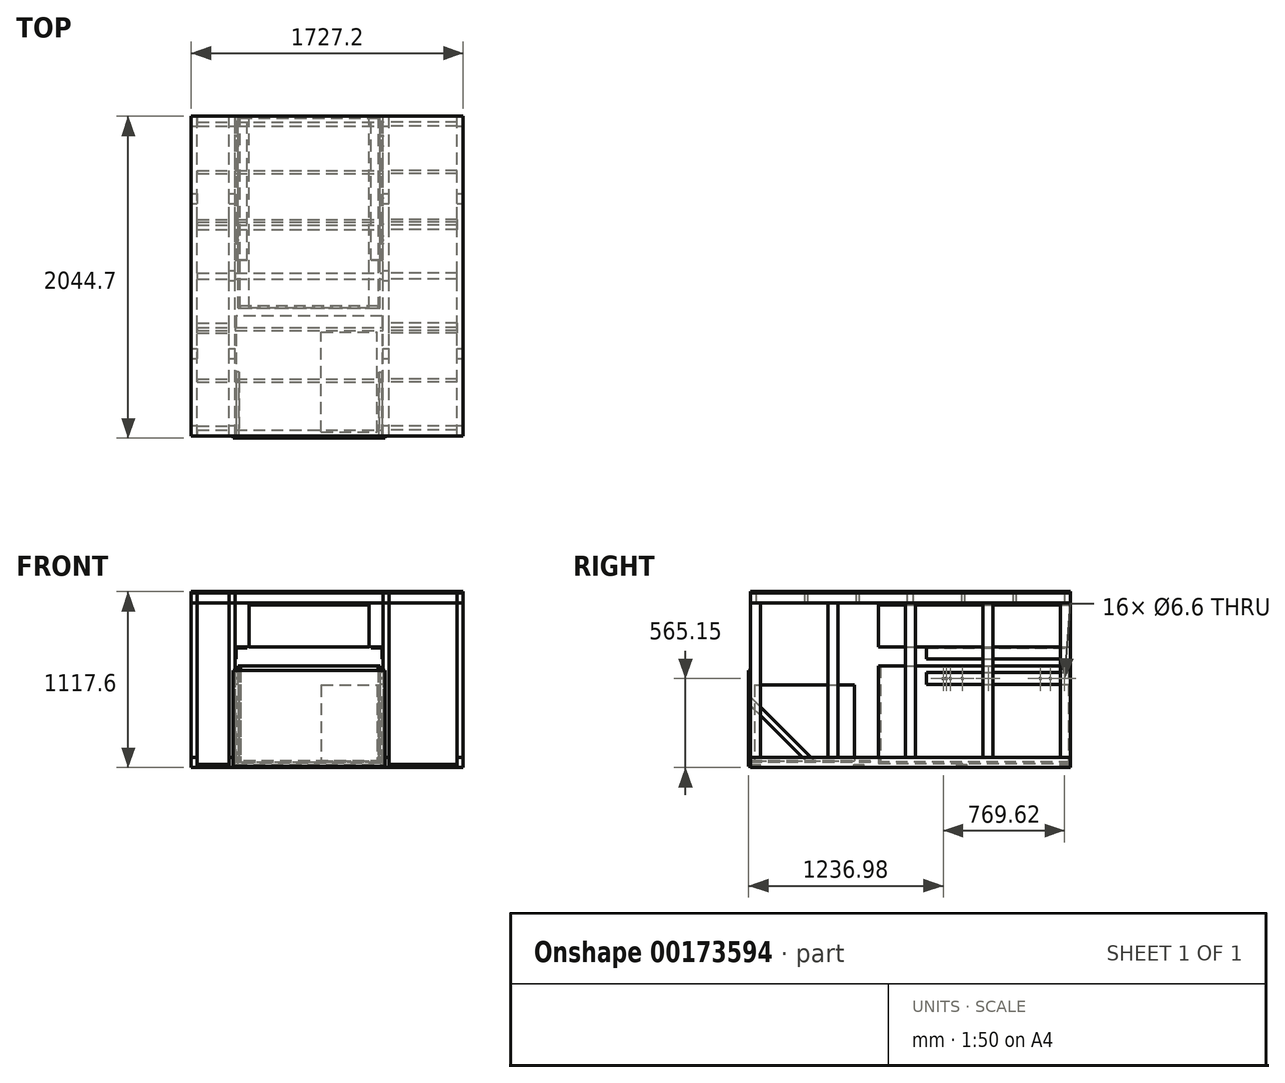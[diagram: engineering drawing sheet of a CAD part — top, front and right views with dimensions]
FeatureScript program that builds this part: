
annotation { "Feature Type Name" : "Feature", "Feature Type Description" : "" }
export const myFeature = defineFeature(function(context is Context, id is Id, definition is map)
    precondition{}
    {
        {
            var Q0;
            Q0=qCreatedBy(makeId("Top.planeOp"),FACE);
            cPlane(context, id + "F0", {"entities" : qUnion([Q0]), "cplaneType" : CPlaneType.OFFSET, "offset" : 1117.6 * mm, "width" : 152.4 * mm, "height" : 152.4 * mm});
        }
        {
            var Q0;
            Q0=qCreatedBy(id+"F0.planeOp",FACE);
            var sketch = newSketch(context, id + "F1", { "sketchPlane" : qUnion([Q0])});
            skLineSegment(sketch, "E0.bottom", {"start": v(-863.6, 1016) * mm, "end": v(863.6, 1016) * mm});
            skLineSegment(sketch, "E0.top", {"start": v(-863.6, -1016) * mm, "end": v(863.6, -1016) * mm});
            skLineSegment(sketch, "E0.left", {"start": v(-863.6, 1016) * mm, "end": v(-863.6, -1016) * mm});
            skLineSegment(sketch, "E0.right", {"start": v(863.6, 1016) * mm, "end": v(863.6, -1016) * mm});
            skPoint(sketch, "E0.middle", {"position": v(0, 0) * mm});
            skSolve(sketch);
        }
        {
            var Q0;
            Q0=makeQuery(id+"F1.imprint","IMPRINT",FACE,{"disambiguationData":[TD([[makeQuery(id+"F1.imprint","IMPRINT",EDGE,{"derivedFrom":sQuery(id+"F1.wireOp",EDGE,"E0.bottom")}),-1.0]])]});
            extrude(context, id + "F2", {"entities" : qUnion([Q0]), "oppositeDirection" : true, "depth" : 9.52 * mm});
        }
        {
            var Q0;
            Q0=makeQuery(id+"F2.opExtrude","SWEPT_FACE",FACE,{"disambiguationData":[OSD([sQuery(id+"F1.wireOp",EDGE,"E0.bottom")])]});
            var sketch = newSketch(context, id + "F3", { "sketchPlane" : qUnion([Q0])});
            skLineSegment(sketch, "E1.bottom", {"start": v(-863.6, 1108.08) * mm, "end": v(-825.5, 1108.08) * mm});
            skLineSegment(sketch, "E1.top", {"start": v(-863.6, 1044.58) * mm, "end": v(-825.5, 1044.58) * mm});
            skLineSegment(sketch, "E1.left", {"start": v(-863.6, 1108.08) * mm, "end": v(-863.6, 1044.58) * mm});
            skLineSegment(sketch, "E1.right", {"start": v(-825.5, 1108.08) * mm, "end": v(-825.5, 1044.58) * mm});
            skLineSegment(sketch, "E2.bottom", {"start": v(863.6, 1108.08) * mm, "end": v(825.5, 1108.08) * mm});
            skLineSegment(sketch, "E2.top", {"start": v(863.6, 1044.58) * mm, "end": v(825.5, 1044.58) * mm});
            skLineSegment(sketch, "E2.left", {"start": v(863.6, 1108.08) * mm, "end": v(863.6, 1044.58) * mm});
            skLineSegment(sketch, "E2.right", {"start": v(825.5, 1108.08) * mm, "end": v(825.5, 1044.58) * mm});
            skLineSegment(sketch, "E3.bottom", {"start": v(-863.6, 0) * mm, "end": v(-825.5, 0) * mm});
            skLineSegment(sketch, "E3.top", {"start": v(-863.6, 63.5) * mm, "end": v(-825.5, 63.5) * mm});
            skLineSegment(sketch, "E3.left", {"start": v(-863.6, 0) * mm, "end": v(-863.6, 63.5) * mm});
            skLineSegment(sketch, "E3.right", {"start": v(-825.5, 0) * mm, "end": v(-825.5, 63.5) * mm});
            skLineSegment(sketch, "E4.bottom", {"start": v(863.6, 0) * mm, "end": v(825.5, 0) * mm});
            skLineSegment(sketch, "E4.top", {"start": v(863.6, 63.5) * mm, "end": v(825.5, 63.5) * mm});
            skLineSegment(sketch, "E4.left", {"start": v(863.6, 0) * mm, "end": v(863.6, 63.5) * mm});
            skLineSegment(sketch, "E4.right", {"start": v(825.5, 0) * mm, "end": v(825.5, 63.5) * mm});
            skLineSegment(sketch, "E5.bottom", {"start": v(-355.6, 1108.08) * mm, "end": v(-393.7, 1108.08) * mm});
            skLineSegment(sketch, "E5.top", {"start": v(-355.6, 1044.58) * mm, "end": v(-393.7, 1044.58) * mm});
            skLineSegment(sketch, "E5.left", {"start": v(-355.6, 1108.08) * mm, "end": v(-355.6, 1044.58) * mm});
            skLineSegment(sketch, "E5.right", {"start": v(-393.7, 1108.08) * mm, "end": v(-393.7, 1044.58) * mm});
            skLineSegment(sketch, "E6.bottom", {"start": v(584.2, 1108.08) * mm, "end": v(622.3, 1108.08) * mm});
            skLineSegment(sketch, "E6.top", {"start": v(584.2, 1044.58) * mm, "end": v(622.3, 1044.58) * mm});
            skLineSegment(sketch, "E6.left", {"start": v(584.2, 1108.08) * mm, "end": v(584.2, 1044.58) * mm});
            skLineSegment(sketch, "E6.right", {"start": v(622.3, 1108.08) * mm, "end": v(622.3, 1044.58) * mm});
            skLineSegment(sketch, "E7.bottom", {"start": v(-355.6, 0) * mm, "end": v(-393.7, 0) * mm});
            skLineSegment(sketch, "E7.top", {"start": v(-355.6, 63.5) * mm, "end": v(-393.7, 63.5) * mm});
            skLineSegment(sketch, "E7.left", {"start": v(-355.6, 0) * mm, "end": v(-355.6, 63.5) * mm});
            skLineSegment(sketch, "E7.right", {"start": v(-393.7, 0) * mm, "end": v(-393.7, 63.5) * mm});
            skLineSegment(sketch, "E8.bottom", {"start": v(622.3, 0) * mm, "end": v(584.2, 0) * mm});
            skLineSegment(sketch, "E8.top", {"start": v(622.3, 63.5) * mm, "end": v(584.2, 63.5) * mm});
            skLineSegment(sketch, "E8.left", {"start": v(622.3, 0) * mm, "end": v(622.3, 63.5) * mm});
            skLineSegment(sketch, "E8.right", {"start": v(584.2, 0) * mm, "end": v(584.2, 63.5) * mm});
            skSolve(sketch);
        }
        {
            var Q0;
            Q0 = qSketchRegion(id + "F3", true);
            var Q1;
            Q1=makeQuery(id+"F2.opExtrude","SWEPT_FACE",FACE,{"disambiguationData":[OSD([sQuery(id+"F1.wireOp",EDGE,"E0.top")])]});
            extrude(context, id + "F4", {"entities" : qUnion([Q0]), "endBound" : BoundingType.UP_TO_SURFACE, "oppositeDirection" : true, "endBoundEntityFace" : qUnion([Q1]), "depth" : 25.4 * mm});
        }
        {
            var Q0;
            Q0=makeQuery(id+"F4.opExtrude","SWEPT_FACE",FACE,{"disambiguationData":[OSD([sQuery(id+"F3.wireOp",EDGE,"E4.top")])]});
            var sketch = newSketch(context, id + "F5", { "sketchPlane" : qUnion([Q0])});
            skLineSegment(sketch, "E9.bottom", {"start": v(863.6, 1016) * mm, "end": v(825.5, 1016) * mm});
            skLineSegment(sketch, "E9.top", {"start": v(863.6, 952.5) * mm, "end": v(825.5, 952.5) * mm});
            skLineSegment(sketch, "E9.left", {"start": v(863.6, 1016) * mm, "end": v(863.6, 952.5) * mm});
            skLineSegment(sketch, "E9.right", {"start": v(825.5, 1016) * mm, "end": v(825.5, 952.5) * mm});
            skLineSegment(sketch, "E10.bottom", {"start": v(863.6, 523.87) * mm, "end": v(825.5, 523.87) * mm});
            skLineSegment(sketch, "E10.top", {"start": v(863.6, 460.37) * mm, "end": v(825.5, 460.37) * mm});
            skLineSegment(sketch, "E10.left", {"start": v(863.6, 523.87) * mm, "end": v(863.6, 460.37) * mm});
            skLineSegment(sketch, "E10.right", {"start": v(825.5, 523.87) * mm, "end": v(825.5, 460.37) * mm});
            skLineSegment(sketch, "E11.bottom", {"start": v(825.5, 31.75) * mm, "end": v(863.6, 31.75) * mm, "construction": true});
            skLineSegment(sketch, "E11.top", {"start": v(825.5, -31.75) * mm, "end": v(863.6, -31.75) * mm, "construction": true});
            skLineSegment(sketch, "E11.left", {"start": v(825.5, 31.75) * mm, "end": v(825.5, -31.75) * mm, "construction": true});
            skLineSegment(sketch, "E11.right", {"start": v(863.6, 31.75) * mm, "end": v(863.6, -31.75) * mm, "construction": true});
            skLineSegment(sketch, "E12.bottom", {"start": v(863.6, -460.38) * mm, "end": v(825.5, -460.38) * mm});
            skLineSegment(sketch, "E12.top", {"start": v(863.6, -523.88) * mm, "end": v(825.5, -523.88) * mm});
            skLineSegment(sketch, "E12.left", {"start": v(863.6, -460.38) * mm, "end": v(863.6, -523.88) * mm});
            skLineSegment(sketch, "E12.right", {"start": v(825.5, -460.38) * mm, "end": v(825.5, -523.88) * mm});
            skLineSegment(sketch, "E13.bottom", {"start": v(825.5, -952.5) * mm, "end": v(863.6, -952.5) * mm});
            skLineSegment(sketch, "E13.top", {"start": v(825.5, -1016) * mm, "end": v(863.6, -1016) * mm});
            skLineSegment(sketch, "E13.left", {"start": v(825.5, -952.5) * mm, "end": v(825.5, -1016) * mm});
            skLineSegment(sketch, "E13.right", {"start": v(863.6, -952.5) * mm, "end": v(863.6, -1016) * mm});
            skLineSegment(sketch, "E14", {"start": v(863.6, 952.5) * mm, "end": v(863.6, 523.87) * mm, "construction": true});
            skLineSegment(sketch, "E15", {"start": v(863.6, 460.37) * mm, "end": v(863.6, 31.75) * mm, "construction": true});
            skLineSegment(sketch, "E16", {"start": v(863.6, -31.75) * mm, "end": v(863.6, -460.38) * mm, "construction": true});
            skLineSegment(sketch, "E17", {"start": v(863.6, -523.88) * mm, "end": v(863.6, -952.5) * mm, "construction": true});
            skPoint(sketch, "E18.0", {"position": v(863.6, 1016) * mm});
            skPoint(sketch, "E18.1", {"position": v(825.5, 1016) * mm});
            skPoint(sketch, "E18.2", {"position": v(863.6, -1016) * mm});
            skPoint(sketch, "E18.3", {"position": v(825.5, -1016) * mm});
            skLineSegment(sketch, "E19.bottom", {"start": v(393.7, 1016) * mm, "end": v(355.6, 1016) * mm});
            skLineSegment(sketch, "E19.top", {"start": v(393.7, 952.5) * mm, "end": v(355.6, 952.5) * mm});
            skLineSegment(sketch, "E19.left", {"start": v(393.7, 1016) * mm, "end": v(393.7, 952.5) * mm});
            skLineSegment(sketch, "E19.right", {"start": v(355.6, 1016) * mm, "end": v(355.6, 952.5) * mm});
            skLineSegment(sketch, "E20.bottom", {"start": v(393.7, 523.87) * mm, "end": v(355.6, 523.87) * mm});
            skLineSegment(sketch, "E20.top", {"start": v(393.7, 460.37) * mm, "end": v(355.6, 460.37) * mm});
            skLineSegment(sketch, "E20.left", {"start": v(393.7, 523.87) * mm, "end": v(393.7, 460.37) * mm});
            skLineSegment(sketch, "E20.right", {"start": v(355.6, 523.87) * mm, "end": v(355.6, 460.37) * mm});
            skLineSegment(sketch, "E21.bottom", {"start": v(355.6, 31.75) * mm, "end": v(393.7, 31.75) * mm});
            skLineSegment(sketch, "E21.top", {"start": v(355.6, -31.75) * mm, "end": v(393.7, -31.75) * mm});
            skLineSegment(sketch, "E21.left", {"start": v(355.6, 31.75) * mm, "end": v(355.6, -31.75) * mm});
            skLineSegment(sketch, "E21.right", {"start": v(393.7, 31.75) * mm, "end": v(393.7, -31.75) * mm});
            skLineSegment(sketch, "E22.bottom", {"start": v(393.7, -460.38) * mm, "end": v(355.6, -460.38) * mm});
            skLineSegment(sketch, "E22.top", {"start": v(393.7, -523.88) * mm, "end": v(355.6, -523.88) * mm});
            skLineSegment(sketch, "E22.left", {"start": v(393.7, -460.38) * mm, "end": v(393.7, -523.88) * mm});
            skLineSegment(sketch, "E22.right", {"start": v(355.6, -460.38) * mm, "end": v(355.6, -523.88) * mm});
            skLineSegment(sketch, "E23.bottom", {"start": v(355.6, -952.5) * mm, "end": v(393.7, -952.5) * mm});
            skLineSegment(sketch, "E23.top", {"start": v(355.6, -1016) * mm, "end": v(393.7, -1016) * mm});
            skLineSegment(sketch, "E23.left", {"start": v(355.6, -952.5) * mm, "end": v(355.6, -1016) * mm});
            skLineSegment(sketch, "E23.right", {"start": v(393.7, -952.5) * mm, "end": v(393.7, -1016) * mm});
            skLineSegment(sketch, "E24", {"start": v(393.7, 952.5) * mm, "end": v(393.7, 523.87) * mm, "construction": true});
            skLineSegment(sketch, "E25", {"start": v(393.7, 460.37) * mm, "end": v(393.7, 31.75) * mm, "construction": true});
            skLineSegment(sketch, "E26", {"start": v(393.7, -31.75) * mm, "end": v(393.7, -460.38) * mm, "construction": true});
            skLineSegment(sketch, "E27", {"start": v(393.7, -523.88) * mm, "end": v(393.7, -952.5) * mm, "construction": true});
            skPoint(sketch, "E28.0", {"position": v(393.7, 1016) * mm});
            skPoint(sketch, "E28.3", {"position": v(355.6, -1016) * mm});
            skPoint(sketch, "E29.0", {"position": v(393.7, -1016) * mm});
            skPoint(sketch, "E29.3", {"position": v(355.6, 1016) * mm});
            skPoint(sketch, "E29.4", {"position": v(-584.2, 1016) * mm});
            skPoint(sketch, "E29.5", {"position": v(-622.3, 1016) * mm});
            skPoint(sketch, "E29.6", {"position": v(-825.5, 1016) * mm});
            skPoint(sketch, "E29.7", {"position": v(-863.6, 1016) * mm});
            skPoint(sketch, "E29.8", {"position": v(-584.2, -1016) * mm});
            skPoint(sketch, "E29.9", {"position": v(-622.3, -1016) * mm});
            skPoint(sketch, "E29.10", {"position": v(-825.5, -1016) * mm});
            skPoint(sketch, "E29.11", {"position": v(-863.6, -1016) * mm});
            skLineSegment(sketch, "E30.bottom", {"start": v(-584.2, 1016) * mm, "end": v(-622.3, 1016) * mm});
            skLineSegment(sketch, "E30.top", {"start": v(-584.2, 952.5) * mm, "end": v(-622.3, 952.5) * mm});
            skLineSegment(sketch, "E30.left", {"start": v(-584.2, 1016) * mm, "end": v(-584.2, 952.5) * mm});
            skLineSegment(sketch, "E30.right", {"start": v(-622.3, 1016) * mm, "end": v(-622.3, 952.5) * mm});
            skLineSegment(sketch, "E31.bottom", {"start": v(-584.2, 523.87) * mm, "end": v(-622.3, 523.87) * mm});
            skLineSegment(sketch, "E31.top", {"start": v(-584.2, 460.37) * mm, "end": v(-622.3, 460.37) * mm});
            skLineSegment(sketch, "E31.left", {"start": v(-584.2, 523.87) * mm, "end": v(-584.2, 460.37) * mm});
            skLineSegment(sketch, "E31.right", {"start": v(-622.3, 523.87) * mm, "end": v(-622.3, 460.37) * mm});
            skLineSegment(sketch, "E32.bottom", {"start": v(-622.3, 31.75) * mm, "end": v(-584.2, 31.75) * mm});
            skLineSegment(sketch, "E32.top", {"start": v(-622.3, -31.75) * mm, "end": v(-584.2, -31.75) * mm});
            skLineSegment(sketch, "E32.left", {"start": v(-622.3, 31.75) * mm, "end": v(-622.3, -31.75) * mm});
            skLineSegment(sketch, "E32.right", {"start": v(-584.2, 31.75) * mm, "end": v(-584.2, -31.75) * mm});
            skLineSegment(sketch, "E33.bottom", {"start": v(-584.2, -460.38) * mm, "end": v(-622.3, -460.38) * mm});
            skLineSegment(sketch, "E33.top", {"start": v(-584.2, -523.88) * mm, "end": v(-622.3, -523.88) * mm});
            skLineSegment(sketch, "E33.left", {"start": v(-584.2, -460.38) * mm, "end": v(-584.2, -523.88) * mm});
            skLineSegment(sketch, "E33.right", {"start": v(-622.3, -460.38) * mm, "end": v(-622.3, -523.88) * mm});
            skLineSegment(sketch, "E34.bottom", {"start": v(-622.3, -952.5) * mm, "end": v(-584.2, -952.5) * mm});
            skLineSegment(sketch, "E34.top", {"start": v(-622.3, -1016) * mm, "end": v(-584.2, -1016) * mm});
            skLineSegment(sketch, "E34.left", {"start": v(-622.3, -952.5) * mm, "end": v(-622.3, -1016) * mm});
            skLineSegment(sketch, "E34.right", {"start": v(-584.2, -952.5) * mm, "end": v(-584.2, -1016) * mm});
            skLineSegment(sketch, "E35", {"start": v(-584.2, 952.5) * mm, "end": v(-584.2, 523.87) * mm, "construction": true});
            skLineSegment(sketch, "E36", {"start": v(-584.2, 460.37) * mm, "end": v(-584.2, 31.75) * mm, "construction": true});
            skLineSegment(sketch, "E37", {"start": v(-584.2, -31.75) * mm, "end": v(-584.2, -460.38) * mm, "construction": true});
            skLineSegment(sketch, "E38", {"start": v(-584.2, -523.88) * mm, "end": v(-584.2, -952.5) * mm, "construction": true});
            skLineSegment(sketch, "E39.bottom", {"start": v(-825.5, 1016) * mm, "end": v(-863.6, 1016) * mm});
            skLineSegment(sketch, "E39.top", {"start": v(-825.5, 952.5) * mm, "end": v(-863.6, 952.5) * mm});
            skLineSegment(sketch, "E39.left", {"start": v(-825.5, 1016) * mm, "end": v(-825.5, 952.5) * mm});
            skLineSegment(sketch, "E39.right", {"start": v(-863.6, 1016) * mm, "end": v(-863.6, 952.5) * mm});
            skLineSegment(sketch, "E40.bottom", {"start": v(-825.5, 523.87) * mm, "end": v(-863.6, 523.87) * mm});
            skLineSegment(sketch, "E40.top", {"start": v(-825.5, 460.37) * mm, "end": v(-863.6, 460.37) * mm});
            skLineSegment(sketch, "E40.left", {"start": v(-825.5, 523.87) * mm, "end": v(-825.5, 460.37) * mm});
            skLineSegment(sketch, "E40.right", {"start": v(-863.6, 523.87) * mm, "end": v(-863.6, 460.37) * mm});
            skLineSegment(sketch, "E41.bottom", {"start": v(-863.6, 31.75) * mm, "end": v(-825.5, 31.75) * mm, "construction": true});
            skLineSegment(sketch, "E41.top", {"start": v(-863.6, -31.75) * mm, "end": v(-825.5, -31.75) * mm, "construction": true});
            skLineSegment(sketch, "E41.left", {"start": v(-863.6, 31.75) * mm, "end": v(-863.6, -31.75) * mm, "construction": true});
            skLineSegment(sketch, "E41.right", {"start": v(-825.5, 31.75) * mm, "end": v(-825.5, -31.75) * mm, "construction": true});
            skLineSegment(sketch, "E42.bottom", {"start": v(-825.5, -460.38) * mm, "end": v(-863.6, -460.38) * mm});
            skLineSegment(sketch, "E42.top", {"start": v(-825.5, -523.88) * mm, "end": v(-863.6, -523.88) * mm});
            skLineSegment(sketch, "E42.left", {"start": v(-825.5, -460.38) * mm, "end": v(-825.5, -523.88) * mm});
            skLineSegment(sketch, "E42.right", {"start": v(-863.6, -460.38) * mm, "end": v(-863.6, -523.88) * mm});
            skLineSegment(sketch, "E43.bottom", {"start": v(-863.6, -952.5) * mm, "end": v(-825.5, -952.5) * mm});
            skLineSegment(sketch, "E43.top", {"start": v(-863.6, -1016) * mm, "end": v(-825.5, -1016) * mm});
            skLineSegment(sketch, "E43.left", {"start": v(-863.6, -952.5) * mm, "end": v(-863.6, -1016) * mm});
            skLineSegment(sketch, "E43.right", {"start": v(-825.5, -952.5) * mm, "end": v(-825.5, -1016) * mm});
            skLineSegment(sketch, "E44", {"start": v(-825.5, 952.5) * mm, "end": v(-825.5, 523.87) * mm, "construction": true});
            skLineSegment(sketch, "E45", {"start": v(-825.5, 460.37) * mm, "end": v(-825.5, 31.75) * mm, "construction": true});
            skLineSegment(sketch, "E46", {"start": v(-825.5, -31.75) * mm, "end": v(-825.5, -460.38) * mm, "construction": true});
            skLineSegment(sketch, "E47", {"start": v(-825.5, -523.88) * mm, "end": v(-825.5, -952.5) * mm, "construction": true});
            skSolve(sketch);
        }
        {
            var Q0;
            Q0 = qSketchRegion(id + "F5", true);
            var Q1;
            Q1=makeQuery(id+"F4.opExtrude","SWEPT_FACE",FACE,{"disambiguationData":[OSD([sQuery(id+"F3.wireOp",EDGE,"E6.top")])]});
            extrude(context, id + "F6", {"entities" : qUnion([Q0]), "endBound" : BoundingType.UP_TO_SURFACE, "endBoundEntityFace" : qUnion([Q1]), "depth" : 25.4 * mm});
        }
        {
            var Q0;
            Q0=makeQuery(id+"F4.opExtrude","SWEPT_FACE",FACE,{"disambiguationData":[OSD([sQuery(id+"F3.wireOp",EDGE,"E7.left")])]});
            var sketch = newSketch(context, id + "F7", { "sketchPlane" : qUnion([Q0])});
            skLineSegment(sketch, "E48.bottom", {"start": v(1016, 0) * mm, "end": v(952.5, 0) * mm, "construction": true});
            skLineSegment(sketch, "E48.top", {"start": v(1016, 19.05) * mm, "end": v(952.5, 19.05) * mm, "construction": true});
            skLineSegment(sketch, "E48.left", {"start": v(1016, 0) * mm, "end": v(1016, 19.05) * mm, "construction": true});
            skLineSegment(sketch, "E48.right", {"start": v(952.5, 0) * mm, "end": v(952.5, 19.05) * mm, "construction": true});
            skLineSegment(sketch, "E49.bottom", {"start": v(359.83, 0) * mm, "end": v(296.33, 0) * mm, "construction": true});
            skLineSegment(sketch, "E49.top", {"start": v(359.83, 19.05) * mm, "end": v(296.33, 19.05) * mm, "construction": true});
            skLineSegment(sketch, "E49.left", {"start": v(359.83, 0) * mm, "end": v(359.83, 19.05) * mm, "construction": true});
            skLineSegment(sketch, "E49.right", {"start": v(296.33, 0) * mm, "end": v(296.33, 19.05) * mm, "construction": true});
            skLineSegment(sketch, "E50.bottom", {"start": v(-296.33, 0) * mm, "end": v(-359.83, 0) * mm});
            skLineSegment(sketch, "E50.top", {"start": v(-296.33, 19.05) * mm, "end": v(-359.83, 19.05) * mm});
            skLineSegment(sketch, "E50.left", {"start": v(-296.33, 0) * mm, "end": v(-296.33, 19.05) * mm});
            skLineSegment(sketch, "E50.right", {"start": v(-359.83, 0) * mm, "end": v(-359.83, 19.05) * mm});
            skLineSegment(sketch, "E51.bottom", {"start": v(-952.5, 0) * mm, "end": v(-1016, 0) * mm});
            skLineSegment(sketch, "E51.top", {"start": v(-952.5, 19.05) * mm, "end": v(-1016, 19.05) * mm});
            skLineSegment(sketch, "E51.left", {"start": v(-952.5, 0) * mm, "end": v(-952.5, 19.05) * mm});
            skLineSegment(sketch, "E51.right", {"start": v(-1016, 0) * mm, "end": v(-1016, 19.05) * mm});
            skLineSegment(sketch, "E52", {"start": v(952.5, 0) * mm, "end": v(359.83, 0) * mm, "construction": true});
            skLineSegment(sketch, "E53", {"start": v(296.33, 0) * mm, "end": v(-296.33, 0) * mm, "construction": true});
            skLineSegment(sketch, "E54", {"start": v(-952.5, 0) * mm, "end": v(-359.83, 0) * mm, "construction": true});
            skPoint(sketch, "E55.0", {"position": v(1016, 1108.07) * mm});
            skLineSegment(sketch, "E56.bottom", {"start": v(1016, 1108.07) * mm, "end": v(977.9, 1108.07) * mm});
            skLineSegment(sketch, "E56.top", {"start": v(1016, 1044.58) * mm, "end": v(977.9, 1044.58) * mm});
            skLineSegment(sketch, "E56.left", {"start": v(1016, 1108.07) * mm, "end": v(1016, 1044.58) * mm});
            skLineSegment(sketch, "E56.right", {"start": v(977.9, 1108.07) * mm, "end": v(977.9, 1044.57) * mm});
            skLineSegment(sketch, "E57.bottom", {"start": v(670.98, 1108.07) * mm, "end": v(651.93, 1108.07) * mm});
            skLineSegment(sketch, "E57.top", {"start": v(670.98, 1044.57) * mm, "end": v(651.93, 1044.57) * mm});
            skLineSegment(sketch, "E57.left", {"start": v(670.98, 1108.07) * mm, "end": v(670.98, 1044.57) * mm});
            skLineSegment(sketch, "E57.right", {"start": v(651.93, 1108.07) * mm, "end": v(651.93, 1044.57) * mm});
            skLineSegment(sketch, "E58.bottom", {"start": v(345.02, 1044.57) * mm, "end": v(325.97, 1044.57) * mm});
            skLineSegment(sketch, "E58.top", {"start": v(345.02, 1108.07) * mm, "end": v(325.97, 1108.07) * mm});
            skLineSegment(sketch, "E58.left", {"start": v(345.02, 1044.57) * mm, "end": v(345.02, 1108.07) * mm});
            skLineSegment(sketch, "E58.right", {"start": v(325.97, 1044.57) * mm, "end": v(325.97, 1108.07) * mm});
            skLineSegment(sketch, "E59.bottom", {"start": v(19.05, 1108.07) * mm, "end": v(-19.05, 1108.07) * mm});
            skLineSegment(sketch, "E59.top", {"start": v(19.05, 1044.57) * mm, "end": v(-19.05, 1044.57) * mm});
            skLineSegment(sketch, "E59.left", {"start": v(19.05, 1108.07) * mm, "end": v(19.05, 1044.57) * mm});
            skLineSegment(sketch, "E59.right", {"start": v(-19.05, 1108.07) * mm, "end": v(-19.05, 1044.57) * mm});
            skLineSegment(sketch, "E60.bottom", {"start": v(-325.97, 1108.07) * mm, "end": v(-345.02, 1108.07) * mm});
            skLineSegment(sketch, "E60.top", {"start": v(-325.97, 1044.57) * mm, "end": v(-345.02, 1044.57) * mm});
            skLineSegment(sketch, "E60.left", {"start": v(-325.97, 1108.07) * mm, "end": v(-325.97, 1044.57) * mm});
            skLineSegment(sketch, "E60.right", {"start": v(-345.02, 1108.07) * mm, "end": v(-345.02, 1044.57) * mm});
            skLineSegment(sketch, "E61.bottom", {"start": v(-651.93, 1108.07) * mm, "end": v(-670.98, 1108.07) * mm});
            skLineSegment(sketch, "E61.top", {"start": v(-651.93, 1044.57) * mm, "end": v(-670.98, 1044.57) * mm});
            skLineSegment(sketch, "E61.left", {"start": v(-651.93, 1108.07) * mm, "end": v(-651.93, 1044.57) * mm});
            skLineSegment(sketch, "E61.right", {"start": v(-670.98, 1108.07) * mm, "end": v(-670.98, 1044.57) * mm});
            skLineSegment(sketch, "E62.bottom", {"start": v(-977.9, 1108.07) * mm, "end": v(-1016, 1108.07) * mm});
            skLineSegment(sketch, "E62.top", {"start": v(-977.9, 1044.57) * mm, "end": v(-1016, 1044.57) * mm});
            skLineSegment(sketch, "E62.left", {"start": v(-977.9, 1108.07) * mm, "end": v(-977.9, 1044.58) * mm});
            skLineSegment(sketch, "E62.right", {"start": v(-1016, 1108.07) * mm, "end": v(-1016, 1044.58) * mm});
            skLineSegment(sketch, "E63", {"start": v(977.9, 1108.07) * mm, "end": v(670.98, 1108.07) * mm, "construction": true});
            skLineSegment(sketch, "E64", {"start": v(651.93, 1108.07) * mm, "end": v(345.02, 1108.07) * mm, "construction": true});
            skLineSegment(sketch, "E65", {"start": v(325.97, 1108.07) * mm, "end": v(19.05, 1108.07) * mm, "construction": true});
            skLineSegment(sketch, "E66", {"start": v(-19.05, 1108.07) * mm, "end": v(-325.97, 1108.07) * mm, "construction": true});
            skLineSegment(sketch, "E67", {"start": v(-345.02, 1108.07) * mm, "end": v(-651.93, 1108.07) * mm, "construction": true});
            skLineSegment(sketch, "E68", {"start": v(-670.98, 1108.07) * mm, "end": v(-977.9, 1108.07) * mm, "construction": true});
            skPoint(sketch, "E69.0", {"position": v(-1016, 1108.07) * mm});
            skSolve(sketch);
        }
        {
            var Q0;
            Q0 = qSketchRegion(id + "F7", true);
            extrude(context, id + "F8", {"entities" : qUnion([Q0]), "endBound" : BoundingType.UP_TO_NEXT, "depth" : 25.4 * mm});
        }
        {
            var Q0;
            Q0=makeQuery(id+"F4.opExtrude","SWEPT_FACE",FACE,{"disambiguationData":[OSD([sQuery(id+"F3.wireOp",EDGE,"E7.right")])]});
            var sketch = newSketch(context, id + "F9", { "sketchPlane" : qUnion([Q0])});
            skLineSegment(sketch, "E70.0", {"start": v(-1016, 0) * mm, "end": v(-952.5, 0) * mm});
            skLineSegment(sketch, "E70.1", {"start": v(-1016, 19.05) * mm, "end": v(-952.5, 19.05) * mm});
            skLineSegment(sketch, "E70.2", {"start": v(-1016, 0) * mm, "end": v(-1016, 19.05) * mm});
            skLineSegment(sketch, "E70.3", {"start": v(-952.5, 0) * mm, "end": v(-952.5, 19.05) * mm});
            skLineSegment(sketch, "E70.4", {"start": v(-359.83, 0) * mm, "end": v(-296.33, 0) * mm});
            skLineSegment(sketch, "E70.5", {"start": v(-359.83, 19.05) * mm, "end": v(-296.33, 19.05) * mm});
            skLineSegment(sketch, "E70.6", {"start": v(-359.83, 0) * mm, "end": v(-359.83, 19.05) * mm});
            skLineSegment(sketch, "E70.7", {"start": v(-296.33, 0) * mm, "end": v(-296.33, 19.05) * mm});
            skLineSegment(sketch, "E70.8", {"start": v(296.33, 0) * mm, "end": v(359.83, 0) * mm});
            skLineSegment(sketch, "E70.9", {"start": v(296.33, 19.05) * mm, "end": v(359.83, 19.05) * mm});
            skLineSegment(sketch, "E70.10", {"start": v(296.33, 0) * mm, "end": v(296.33, 19.05) * mm});
            skLineSegment(sketch, "E70.11", {"start": v(359.83, 0) * mm, "end": v(359.83, 19.05) * mm});
            skLineSegment(sketch, "E70.12", {"start": v(952.5, 0) * mm, "end": v(1016, 0) * mm});
            skLineSegment(sketch, "E70.13", {"start": v(952.5, 19.05) * mm, "end": v(1016, 19.05) * mm});
            skLineSegment(sketch, "E70.14", {"start": v(952.5, 0) * mm, "end": v(952.5, 19.05) * mm});
            skLineSegment(sketch, "E70.15", {"start": v(1016, 0) * mm, "end": v(1016, 19.05) * mm});
            skLineSegment(sketch, "E70.16", {"start": v(-952.5, 0) * mm, "end": v(-359.83, 0) * mm});
            skLineSegment(sketch, "E70.17", {"start": v(-296.33, 0) * mm, "end": v(296.33, 0) * mm});
            skLineSegment(sketch, "E70.18", {"start": v(952.5, 0) * mm, "end": v(359.83, 0) * mm});
            skPoint(sketch, "E70.19", {"position": v(-1016, 1108.07) * mm});
            skLineSegment(sketch, "E70.20", {"start": v(-1016, 1108.07) * mm, "end": v(-977.9, 1108.07) * mm});
            skLineSegment(sketch, "E70.21", {"start": v(-1016, 1044.58) * mm, "end": v(-977.9, 1044.58) * mm});
            skLineSegment(sketch, "E70.22", {"start": v(-1016, 1108.07) * mm, "end": v(-1016, 1044.58) * mm});
            skLineSegment(sketch, "E70.23", {"start": v(-977.9, 1108.07) * mm, "end": v(-977.9, 1044.57) * mm});
            skLineSegment(sketch, "E70.24", {"start": v(-670.98, 1108.07) * mm, "end": v(-651.93, 1108.07) * mm});
            skLineSegment(sketch, "E70.25", {"start": v(-670.98, 1044.57) * mm, "end": v(-651.93, 1044.57) * mm});
            skLineSegment(sketch, "E70.26", {"start": v(-670.98, 1108.07) * mm, "end": v(-670.98, 1044.57) * mm});
            skLineSegment(sketch, "E70.27", {"start": v(-651.93, 1108.07) * mm, "end": v(-651.93, 1044.57) * mm});
            skLineSegment(sketch, "E70.28", {"start": v(-345.02, 1044.57) * mm, "end": v(-325.97, 1044.57) * mm});
            skLineSegment(sketch, "E70.29", {"start": v(-345.02, 1108.07) * mm, "end": v(-325.97, 1108.07) * mm});
            skLineSegment(sketch, "E70.30", {"start": v(-345.02, 1044.57) * mm, "end": v(-345.02, 1108.07) * mm});
            skLineSegment(sketch, "E70.31", {"start": v(-325.97, 1044.57) * mm, "end": v(-325.97, 1108.07) * mm});
            skLineSegment(sketch, "E70.32", {"start": v(-19.05, 1108.07) * mm, "end": v(19.05, 1108.07) * mm});
            skLineSegment(sketch, "E70.33", {"start": v(-19.05, 1044.57) * mm, "end": v(19.05, 1044.57) * mm});
            skLineSegment(sketch, "E70.34", {"start": v(-19.05, 1108.07) * mm, "end": v(-19.05, 1044.57) * mm});
            skLineSegment(sketch, "E70.35", {"start": v(19.05, 1108.07) * mm, "end": v(19.05, 1044.57) * mm});
            skLineSegment(sketch, "E70.40", {"start": v(325.97, 1108.07) * mm, "end": v(345.02, 1108.07) * mm});
            skLineSegment(sketch, "E70.41", {"start": v(325.97, 1044.57) * mm, "end": v(345.02, 1044.57) * mm});
            skLineSegment(sketch, "E70.42", {"start": v(325.97, 1108.07) * mm, "end": v(325.97, 1044.57) * mm});
            skLineSegment(sketch, "E70.43", {"start": v(345.02, 1108.07) * mm, "end": v(345.02, 1044.57) * mm});
            skLineSegment(sketch, "E70.44", {"start": v(651.93, 1108.07) * mm, "end": v(670.98, 1108.07) * mm});
            skLineSegment(sketch, "E70.45", {"start": v(651.93, 1044.57) * mm, "end": v(670.98, 1044.57) * mm});
            skLineSegment(sketch, "E70.46", {"start": v(651.93, 1108.07) * mm, "end": v(651.93, 1044.57) * mm});
            skLineSegment(sketch, "E70.47", {"start": v(670.98, 1108.07) * mm, "end": v(670.98, 1044.57) * mm});
            skLineSegment(sketch, "E70.48", {"start": v(977.9, 1108.07) * mm, "end": v(1016, 1108.07) * mm});
            skLineSegment(sketch, "E70.49", {"start": v(977.9, 1044.57) * mm, "end": v(1016, 1044.57) * mm});
            skLineSegment(sketch, "E70.50", {"start": v(977.9, 1108.07) * mm, "end": v(977.9, 1044.58) * mm});
            skLineSegment(sketch, "E70.51", {"start": v(1016, 1108.07) * mm, "end": v(1016, 1044.58) * mm});
            skLineSegment(sketch, "E70.52", {"start": v(-977.9, 1108.07) * mm, "end": v(-670.98, 1108.07) * mm});
            skLineSegment(sketch, "E70.53", {"start": v(-651.93, 1108.07) * mm, "end": v(-345.02, 1108.07) * mm});
            skLineSegment(sketch, "E70.54", {"start": v(-325.97, 1108.07) * mm, "end": v(-19.05, 1108.07) * mm});
            skLineSegment(sketch, "E70.55", {"start": v(19.05, 1108.07) * mm, "end": v(325.97, 1108.07) * mm});
            skLineSegment(sketch, "E70.57", {"start": v(345.02, 1108.07) * mm, "end": v(651.93, 1108.07) * mm});
            skLineSegment(sketch, "E70.58", {"start": v(670.98, 1108.07) * mm, "end": v(977.9, 1108.07) * mm});
            skPoint(sketch, "E70.59", {"position": v(1016, 1108.07) * mm});
            skSolve(sketch);
        }
        {
            var Q0;
            Q0 = qSketchRegion(id + "F9", true);
            extrude(context, id + "F10", {"entities" : qUnion([Q0]), "endBound" : BoundingType.UP_TO_NEXT, "depth" : 25.4 * mm});
        }
        {
            var Q0;
            Q0=makeQuery(id+"F4.opExtrude","SWEPT_FACE",FACE,{"disambiguationData":[OSD([sQuery(id+"F3.wireOp",EDGE,"E8.left")])]});
            var sketch = newSketch(context, id + "F11", { "sketchPlane" : qUnion([Q0])});
            skLineSegment(sketch, "E71.0", {"start": v(1016, 0) * mm, "end": v(952.5, 0) * mm});
            skLineSegment(sketch, "E71.1", {"start": v(1016, 19.05) * mm, "end": v(952.5, 19.05) * mm});
            skLineSegment(sketch, "E71.2", {"start": v(1016, 0) * mm, "end": v(1016, 19.05) * mm});
            skLineSegment(sketch, "E71.3", {"start": v(952.5, 0) * mm, "end": v(952.5, 19.05) * mm});
            skLineSegment(sketch, "E71.4", {"start": v(359.83, 0) * mm, "end": v(296.33, 0) * mm});
            skLineSegment(sketch, "E71.5", {"start": v(359.83, 19.05) * mm, "end": v(296.33, 19.05) * mm});
            skLineSegment(sketch, "E71.6", {"start": v(359.83, 0) * mm, "end": v(359.83, 19.05) * mm});
            skLineSegment(sketch, "E71.7", {"start": v(296.33, 0) * mm, "end": v(296.33, 19.05) * mm});
            skLineSegment(sketch, "E71.8", {"start": v(-296.33, 0) * mm, "end": v(-359.83, 0) * mm});
            skLineSegment(sketch, "E71.9", {"start": v(-296.33, 19.05) * mm, "end": v(-359.83, 19.05) * mm});
            skLineSegment(sketch, "E71.10", {"start": v(-296.33, 0) * mm, "end": v(-296.33, 19.05) * mm});
            skLineSegment(sketch, "E71.11", {"start": v(-359.83, 0) * mm, "end": v(-359.83, 19.05) * mm});
            skLineSegment(sketch, "E71.12", {"start": v(-952.5, 0) * mm, "end": v(-1016, 0) * mm});
            skLineSegment(sketch, "E71.13", {"start": v(-952.5, 19.05) * mm, "end": v(-1016, 19.05) * mm});
            skLineSegment(sketch, "E71.14", {"start": v(-952.5, 0) * mm, "end": v(-952.5, 19.05) * mm});
            skLineSegment(sketch, "E71.15", {"start": v(-1016, 0) * mm, "end": v(-1016, 19.05) * mm});
            skLineSegment(sketch, "E71.16", {"start": v(952.5, 0) * mm, "end": v(359.83, 0) * mm});
            skLineSegment(sketch, "E71.17", {"start": v(296.33, 0) * mm, "end": v(-296.33, 0) * mm});
            skLineSegment(sketch, "E71.18", {"start": v(-952.5, 0) * mm, "end": v(-359.83, 0) * mm});
            skPoint(sketch, "E71.19", {"position": v(1016, 1108.07) * mm});
            skLineSegment(sketch, "E71.20", {"start": v(1016, 1108.07) * mm, "end": v(977.9, 1108.07) * mm});
            skLineSegment(sketch, "E71.21", {"start": v(1016, 1044.58) * mm, "end": v(977.9, 1044.58) * mm});
            skLineSegment(sketch, "E71.22", {"start": v(1016, 1108.08) * mm, "end": v(1016, 1044.58) * mm});
            skLineSegment(sketch, "E71.23", {"start": v(977.9, 1108.07) * mm, "end": v(977.9, 1044.58) * mm});
            skLineSegment(sketch, "E71.24", {"start": v(670.98, 1108.07) * mm, "end": v(651.93, 1108.07) * mm});
            skLineSegment(sketch, "E71.25", {"start": v(670.98, 1044.57) * mm, "end": v(651.93, 1044.57) * mm});
            skLineSegment(sketch, "E71.26", {"start": v(670.98, 1108.08) * mm, "end": v(670.98, 1044.58) * mm});
            skLineSegment(sketch, "E71.27", {"start": v(651.93, 1108.08) * mm, "end": v(651.93, 1044.58) * mm});
            skLineSegment(sketch, "E71.28", {"start": v(345.02, 1044.57) * mm, "end": v(325.97, 1044.57) * mm});
            skLineSegment(sketch, "E71.29", {"start": v(345.02, 1108.07) * mm, "end": v(325.97, 1108.07) * mm});
            skLineSegment(sketch, "E71.30", {"start": v(345.02, 1044.58) * mm, "end": v(345.02, 1108.08) * mm});
            skLineSegment(sketch, "E71.31", {"start": v(325.97, 1044.58) * mm, "end": v(325.97, 1108.08) * mm});
            skLineSegment(sketch, "E71.32", {"start": v(19.05, 1108.07) * mm, "end": v(-19.05, 1108.07) * mm});
            skLineSegment(sketch, "E71.33", {"start": v(19.05, 1044.57) * mm, "end": v(-19.05, 1044.57) * mm});
            skLineSegment(sketch, "E71.34", {"start": v(19.05, 1108.08) * mm, "end": v(19.05, 1044.58) * mm});
            skLineSegment(sketch, "E71.35", {"start": v(-19.05, 1108.08) * mm, "end": v(-19.05, 1044.58) * mm});
            skLineSegment(sketch, "E71.40", {"start": v(-325.97, 1108.07) * mm, "end": v(-345.02, 1108.07) * mm});
            skLineSegment(sketch, "E71.41", {"start": v(-325.97, 1044.57) * mm, "end": v(-345.02, 1044.57) * mm});
            skLineSegment(sketch, "E71.42", {"start": v(-325.97, 1108.08) * mm, "end": v(-325.97, 1044.58) * mm});
            skLineSegment(sketch, "E71.43", {"start": v(-345.02, 1108.08) * mm, "end": v(-345.02, 1044.58) * mm});
            skLineSegment(sketch, "E71.44", {"start": v(-651.93, 1108.07) * mm, "end": v(-670.98, 1108.07) * mm});
            skLineSegment(sketch, "E71.45", {"start": v(-651.93, 1044.57) * mm, "end": v(-670.98, 1044.57) * mm});
            skLineSegment(sketch, "E71.46", {"start": v(-651.93, 1108.08) * mm, "end": v(-651.93, 1044.58) * mm});
            skLineSegment(sketch, "E71.47", {"start": v(-670.98, 1108.08) * mm, "end": v(-670.98, 1044.58) * mm});
            skLineSegment(sketch, "E71.48", {"start": v(-977.9, 1108.07) * mm, "end": v(-1016, 1108.07) * mm});
            skLineSegment(sketch, "E71.49", {"start": v(-977.9, 1044.57) * mm, "end": v(-1016, 1044.57) * mm});
            skLineSegment(sketch, "E71.50", {"start": v(-977.9, 1108.08) * mm, "end": v(-977.9, 1044.58) * mm});
            skLineSegment(sketch, "E71.51", {"start": v(-1016, 1108.08) * mm, "end": v(-1016, 1044.58) * mm});
            skLineSegment(sketch, "E71.52", {"start": v(977.9, 1108.07) * mm, "end": v(670.98, 1108.07) * mm});
            skLineSegment(sketch, "E71.53", {"start": v(651.93, 1108.07) * mm, "end": v(345.02, 1108.07) * mm});
            skLineSegment(sketch, "E71.54", {"start": v(325.97, 1108.07) * mm, "end": v(19.05, 1108.07) * mm});
            skLineSegment(sketch, "E71.55", {"start": v(-19.05, 1108.07) * mm, "end": v(-325.97, 1108.07) * mm});
            skLineSegment(sketch, "E71.57", {"start": v(-345.02, 1108.07) * mm, "end": v(-651.93, 1108.07) * mm});
            skLineSegment(sketch, "E71.58", {"start": v(-670.98, 1108.07) * mm, "end": v(-977.9, 1108.07) * mm});
            skPoint(sketch, "E71.59", {"position": v(-1016, 1108.07) * mm});
            skSolve(sketch);
        }
        {
            var Q0;
            Q0 = qSketchRegion(id + "F11", true);
            extrude(context, id + "F12", {"entities" : qUnion([Q0]), "endBound" : BoundingType.UP_TO_NEXT, "depth" : 25.4 * mm});
        }
        {
            var Q0;
            Q0=makeQuery(id+"F6.opExtrude","SWEPT_FACE",FACE,{"disambiguationData":[OSD([sQuery(id+"F5.wireOp",EDGE,"E19.bottom")])]});
            var sketch = newSketch(context, id + "F13", { "sketchPlane" : qUnion([Q0])});
            skLineSegment(sketch, "E72.bottom", {"start": v(-355.6, 603.25) * mm, "end": v(-336.55, 603.25) * mm});
            skLineSegment(sketch, "E72.top", {"start": v(-355.6, 527.05) * mm, "end": v(-336.55, 527.05) * mm});
            skLineSegment(sketch, "E72.left", {"start": v(-355.6, 603.25) * mm, "end": v(-355.6, 527.05) * mm});
            skLineSegment(sketch, "E72.right", {"start": v(-336.55, 603.25) * mm, "end": v(-336.55, 527.05) * mm});
            skLineSegment(sketch, "E73.0", {"start": v(584.2, 1044.58) * mm, "end": v(584.2, 63.5) * mm, "construction": true});
            skLineSegment(sketch, "E74.bottom", {"start": v(565.15, 527.05) * mm, "end": v(584.2, 527.05) * mm});
            skLineSegment(sketch, "E74.top", {"start": v(565.15, 603.25) * mm, "end": v(584.2, 603.25) * mm});
            skLineSegment(sketch, "E74.left", {"start": v(565.15, 527.05) * mm, "end": v(565.15, 603.25) * mm});
            skLineSegment(sketch, "E74.right", {"start": v(584.2, 527.05) * mm, "end": v(584.2, 603.25) * mm});
            skLineSegment(sketch, "E75", {"start": v(-355.6, 531.81) * mm, "end": v(584.2, 531.81) * mm, "construction": true});
            skLineSegment(sketch, "E76", {"start": v(0, 19.05) * mm, "end": v(0, 1044.58) * mm, "construction": true});
            skPoint(sketch, "E77", {"position": v(0, 531.81) * mm});
            skSolve(sketch);
        }
        {
            var Q0;
            Q0 = qSketchRegion(id + "F13", true);
            extrude(context, id + "F14", {"entities" : qUnion([Q0]), "oppositeDirection" : true, "depth" : 914.4 * mm});
        }
        {
            var Q0;
            Q0=makeQuery(id+"F14.opExtrude","SWEPT_FACE",FACE,{"disambiguationData":[OSD([sQuery(id+"F13.wireOp",EDGE,"E72.right")])]});
            var sketch = newSketch(context, id + "F15", { "sketchPlane" : qUnion([Q0])});
            skLineSegment(sketch, "E78", {"start": v(-977.9, 603.25) * mm, "end": v(-977.9, 527.05) * mm, "construction": true});
            skLineSegment(sketch, "E79", {"start": v(-889, 603.25) * mm, "end": v(-889, 527.05) * mm, "construction": true});
            skLineSegment(sketch, "E80", {"start": v(-825.5, 603.25) * mm, "end": v(-825.5, 527.05) * mm, "construction": true});
            skLineSegment(sketch, "E81", {"start": v(-495.3, 603.25) * mm, "end": v(-495.3, 527.05) * mm, "construction": true});
            skLineSegment(sketch, "E82", {"start": v(-330.2, 603.25) * mm, "end": v(-330.2, 527.05) * mm, "construction": true});
            skLineSegment(sketch, "E83", {"start": v(-254, 603.25) * mm, "end": v(-254, 527.05) * mm, "construction": true});
            skLineSegment(sketch, "E84", {"start": v(-228.6, 603.25) * mm, "end": v(-228.6, 527.05) * mm, "construction": true});
            skLineSegment(sketch, "E85", {"start": v(-208.28, 603.25) * mm, "end": v(-208.28, 527.05) * mm, "construction": true});
            skCircle(sketch, "E86", {"center": v(-977.9, 565.15) * mm, "radius": 3.3 * mm});
            skCircle(sketch, "E87", {"center": v(-889, 565.15) * mm, "radius": 3.3 * mm});
            skCircle(sketch, "E88", {"center": v(-825.5, 565.15) * mm, "radius": 3.3 * mm});
            skCircle(sketch, "E89", {"center": v(-495.3, 565.15) * mm, "radius": 3.3 * mm});
            skCircle(sketch, "E90", {"center": v(-330.2, 565.15) * mm, "radius": 3.3 * mm});
            skCircle(sketch, "E91", {"center": v(-254, 565.15) * mm, "radius": 3.3 * mm});
            skCircle(sketch, "E92", {"center": v(-228.6, 565.15) * mm, "radius": 3.3 * mm});
            skCircle(sketch, "E93", {"center": v(-208.28, 565.15) * mm, "radius": 3.3 * mm});
            skSolve(sketch);
        }
        {
            var Q0;
            Q0 = qSketchRegion(id + "F15", true);
            var Q1;
            Q1=makeQuery(id+"F14.opExtrude","SWEPT_FACE",FACE,{"disambiguationData":[OSD([sQuery(id+"F13.wireOp",EDGE,"E72.left")])]});
            var Q2;
            Q2=makeQuery(id+"F14.opExtrude","SWEPT_FACE",FACE,{"disambiguationData":[OSD([sQuery(id+"F13.wireOp",EDGE,"E74.right")])]});
            extrude(context, id + "F16", {"entities" : qUnion([Q0]), "operationType" : NewBodyOperationType.REMOVE, "endBound" : BoundingType.UP_TO_SURFACE, "oppositeDirection" : true, "endBoundEntityFace" : qUnion([Q1]), "depth" : 25.4 * mm, "hasSecondDirection" : true, "secondDirectionBound" : SecondDirectionBoundingType.UP_TO_SURFACE, "secondDirectionOppositeDirection" : false, "secondDirectionBoundEntityFace" : qUnion([Q2]), "secondDirectionDepth" : 25.4 * mm});
        }
        {
            var Q0;
            Q0=makeQuery(id+"F6.opExtrude","SWEPT_FACE",FACE,{"disambiguationData":[OSD([sQuery(id+"F5.wireOp",EDGE,"E19.bottom")])]});
            var sketch = newSketch(context, id + "F17", { "sketchPlane" : qUnion([Q0])});
            skLineSegment(sketch, "E94", {"start": v(-336.55, 34.92) * mm, "end": v(-336.55, 25.4) * mm});
            skLineSegment(sketch, "E95", {"start": v(-336.55, 25.4) * mm, "end": v(565.15, 25.4) * mm});
            skLineSegment(sketch, "E96", {"start": v(565.15, 25.4) * mm, "end": v(565.15, 34.92) * mm});
            skLineSegment(sketch, "E97", {"start": v(565.15, 34.92) * mm, "end": v(-336.55, 34.92) * mm});
            skLineSegment(sketch, "E98.0", {"start": v(584.2, 19.05) * mm, "end": v(-355.6, 19.05) * mm, "construction": true});
            skLineSegment(sketch, "E99.0", {"start": v(-336.55, 603.25) * mm, "end": v(-336.55, 527.05) * mm, "construction": true});
            skLineSegment(sketch, "E99.1", {"start": v(565.15, 527.05) * mm, "end": v(565.15, 603.25) * mm, "construction": true});
            skSolve(sketch);
        }
        {
            var Q0;
            Q0 = qSketchRegion(id + "F17", true);
            extrude(context, id + "F18", {"entities" : qUnion([Q0]), "oppositeDirection" : true, "depth" : 1219.2 * mm});
        }
        {
            var Q0;
            Q0=makeQuery(id+"F18.opExtrude","SWEPT_FACE",FACE,{"disambiguationData":[OSD([sQuery(id+"F17.wireOp",EDGE,"E97")])]});
            var sketch = newSketch(context, id + "F19", { "sketchPlane" : qUnion([Q0])});
            skLineSegment(sketch, "E100.bottom", {"start": v(336.55, 1016) * mm, "end": v(323.85, 1016) * mm});
            skLineSegment(sketch, "E100.top", {"start": v(336.55, -203.2) * mm, "end": v(323.85, -203.2) * mm});
            skLineSegment(sketch, "E100.left", {"start": v(336.55, 1016) * mm, "end": v(336.55, -203.2) * mm});
            skLineSegment(sketch, "E100.right", {"start": v(323.85, 1016) * mm, "end": v(323.85, -203.2) * mm});
            skLineSegment(sketch, "E101.bottom", {"start": v(323.6, -203.2) * mm, "end": v(-552.2, -203.2) * mm});
            skLineSegment(sketch, "E101.top", {"start": v(323.6, -190.5) * mm, "end": v(-552.2, -190.5) * mm});
            skLineSegment(sketch, "E101.left", {"start": v(323.6, -203.2) * mm, "end": v(323.6, -190.5) * mm});
            skLineSegment(sketch, "E101.right", {"start": v(-552.2, -203.2) * mm, "end": v(-552.2, -190.5) * mm});
            skLineSegment(sketch, "E102.bottom", {"start": v(-565.15, -203.2) * mm, "end": v(-552.45, -203.2) * mm});
            skLineSegment(sketch, "E102.top", {"start": v(-565.15, 1016) * mm, "end": v(-552.45, 1016) * mm});
            skLineSegment(sketch, "E102.left", {"start": v(-565.15, -203.2) * mm, "end": v(-565.15, 1016) * mm});
            skLineSegment(sketch, "E102.right", {"start": v(-552.45, -203.2) * mm, "end": v(-552.45, 1016) * mm});
            skLineSegment(sketch, "E103.bottom", {"start": v(-552.2, 1016) * mm, "end": v(323.6, 1016) * mm});
            skLineSegment(sketch, "E103.top", {"start": v(-552.2, 1003.3) * mm, "end": v(323.6, 1003.3) * mm});
            skLineSegment(sketch, "E103.left", {"start": v(-552.2, 1016) * mm, "end": v(-552.2, 1003.3) * mm});
            skLineSegment(sketch, "E103.right", {"start": v(323.6, 1016) * mm, "end": v(323.6, 1003.3) * mm});
            skSolve(sketch);
        }
        {
            var Q0;
            Q0 = qSketchRegion(id + "F19", true);
            extrude(context, id + "F20", {"entities" : qUnion([Q0]), "depth" : 609.6 * mm});
        }
        {
            var Q0;
            Q0=makeQuery(id+"F6.opExtrude","SWEPT_FACE",FACE,{"disambiguationData":[OSD([sQuery(id+"F5.wireOp",EDGE,"E19.bottom")])]});
            var sketch = newSketch(context, id + "F21", { "sketchPlane" : qUnion([Q0])});
            skLineSegment(sketch, "E104.bottom", {"start": v(-266.7, 765.18) * mm, "end": v(495.3, 765.18) * mm});
            skLineSegment(sketch, "E104.top", {"start": v(-266.7, 1031.88) * mm, "end": v(495.3, 1031.88) * mm});
            skLineSegment(sketch, "E104.left", {"start": v(-266.7, 765.18) * mm, "end": v(-266.7, 1031.88) * mm});
            skLineSegment(sketch, "E104.right", {"start": v(495.3, 765.18) * mm, "end": v(495.3, 1031.88) * mm});
            skPoint(sketch, "E105", {"position": v(114.3, 1044.58) * mm});
            skLineSegment(sketch, "E106", {"start": v(114.3, 1044.58) * mm, "end": v(114.3, 1031.88) * mm, "construction": true});
            skSolve(sketch);
        }
        {
            var Q0;
            Q0=makeQuery(id+"F21.imprint","IMPRINT",FACE,{"disambiguationData":[TD([[makeQuery(id+"F21.imprint","IMPRINT",EDGE,{"derivedFrom":sQuery(id+"F21.wireOp",EDGE,"E104.bottom")}),1.0]])]});
            extrude(context, id + "F22", {"entities" : qUnion([Q0]), "oppositeDirection" : true, "depth" : 1219.2 * mm});
        }
        {
            var Q0;
            Q0=makeQuery(id+"F22.opExtrude","CAP_FACE",FACE,{"disambiguationData":[OSD([sQuery(id+"F21.wireOp",EDGE,"E104.bottom"),sQuery(id+"F21.wireOp",EDGE,"E104.top"),sQuery(id+"F21.wireOp",EDGE,"E104.left"),sQuery(id+"F21.wireOp",EDGE,"E104.right")])],"isStart":true});
            var sketch = newSketch(context, id + "F23", { "sketchPlane" : qUnion([Q0])});
            skLineSegment(sketch, "E107", {"start": v(-279.4, 765.18) * mm, "end": v(-279.4, 758.83) * mm});
            skLineSegment(sketch, "E108", {"start": v(-279.4, 758.83) * mm, "end": v(-349.25, 758.83) * mm});
            skLineSegment(sketch, "E109", {"start": v(-349.25, 758.83) * mm, "end": v(-349.25, 688.98) * mm});
            skLineSegment(sketch, "E110.0", {"start": v(-355.6, 1044.58) * mm, "end": v(-355.6, 63.5) * mm, "construction": true});
            skLineSegment(sketch, "E110.1", {"start": v(584.2, 1044.58) * mm, "end": v(584.2, 63.5) * mm, "construction": true});
            skLineSegment(sketch, "E111", {"start": v(-349.25, 688.98) * mm, "end": v(-355.6, 688.98) * mm});
            skLineSegment(sketch, "E112", {"start": v(-355.6, 688.98) * mm, "end": v(-355.6, 765.18) * mm});
            skLineSegment(sketch, "E113", {"start": v(-355.6, 765.18) * mm, "end": v(-279.4, 765.18) * mm});
            skLineSegment(sketch, "E114", {"start": v(-355.6, 1044.58) * mm, "end": v(584.2, 1044.58) * mm, "construction": true});
            skLineSegment(sketch, "E115", {"start": v(114.3, 901.31) * mm, "end": v(114.3, 1044.58) * mm, "construction": true});
            skLineSegment(sketch, "E116.MirrorCS", {"start": v(577.85, 688.98) * mm, "end": v(584.2, 688.98) * mm});
            skLineSegment(sketch, "E117.MirrorCS", {"start": v(508, 765.18) * mm, "end": v(508, 758.83) * mm});
            skLineSegment(sketch, "E118.MirrorCS", {"start": v(584.2, 765.18) * mm, "end": v(508, 765.18) * mm});
            skLineSegment(sketch, "E119.MirrorCS", {"start": v(584.2, 688.98) * mm, "end": v(584.2, 765.18) * mm});
            skLineSegment(sketch, "E120.MirrorCS", {"start": v(508, 758.83) * mm, "end": v(577.85, 758.83) * mm});
            skLineSegment(sketch, "E121.MirrorCS", {"start": v(577.85, 758.83) * mm, "end": v(577.85, 688.98) * mm});
            skSolve(sketch);
        }
        {
            var Q0;
            Q0 = qSketchRegion(id + "F23", true);
            extrude(context, id + "F24", {"entities" : qUnion([Q0]), "oppositeDirection" : true, "depth" : 914.4 * mm});
        }
        {
            var Q0;
            Q0=makeQuery(id+"F6.opExtrude","SWEPT_FACE",FACE,{"disambiguationData":[OSD([sQuery(id+"F5.wireOp",EDGE,"E23.top")])]});
            var sketch = newSketch(context, id + "F25", { "sketchPlane" : qUnion([Q0])});
            skLineSegment(sketch, "E122.bottom", {"start": v(349.25, 31.75) * mm, "end": v(-577.85, 31.75) * mm});
            skLineSegment(sketch, "E122.top", {"start": v(349.25, 41.28) * mm, "end": v(-577.85, 41.27) * mm});
            skLineSegment(sketch, "E122.left", {"start": v(349.25, 31.75) * mm, "end": v(349.25, 41.28) * mm});
            skLineSegment(sketch, "E122.right", {"start": v(-577.85, 31.75) * mm, "end": v(-577.85, 41.27) * mm});
            skSolve(sketch);
        }
        {
            var Q0;
            Q0 = qSketchRegion(id + "F25", true);
            extrude(context, id + "F26", {"entities" : qUnion([Q0]), "oppositeDirection" : true, "depth" : 762 * mm});
        }
        {
            var Q0;
            Q0=makeQuery(id+"F26.opExtrude","CAP_FACE",FACE,{"disambiguationData":[OSD([sQuery(id+"F25.wireOp",EDGE,"E122.bottom"),sQuery(id+"F25.wireOp",EDGE,"E122.top"),sQuery(id+"F25.wireOp",EDGE,"E122.left"),sQuery(id+"F25.wireOp",EDGE,"E122.right")])],"isStart":true});
            var sketch = newSketch(context, id + "F27", { "sketchPlane" : qUnion([Q0])});
            skLineSegment(sketch, "E123.bottom", {"start": v(-596.9, 6.35) * mm, "end": v(368.3, 6.35) * mm});
            skLineSegment(sketch, "E123.top", {"start": v(-596.9, 615.95) * mm, "end": v(368.3, 615.95) * mm});
            skLineSegment(sketch, "E123.left", {"start": v(-596.9, 6.35) * mm, "end": v(-596.9, 615.95) * mm});
            skLineSegment(sketch, "E123.right", {"start": v(368.3, 6.35) * mm, "end": v(368.3, 615.95) * mm});
            skLineSegment(sketch, "E124", {"start": v(-114.3, 41.28) * mm, "end": v(-114.3, 6.35) * mm, "construction": true});
            skSolve(sketch);
        }
        {
            var Q0;
            Q0 = qSketchRegion(id + "F27", true);
            extrude(context, id + "F28", {"entities" : qUnion([Q0]), "depth" : 12.7 * mm});
        }
        {
            var Q0;
            Q0=makeQuery(id+"F26.opExtrude","SWEPT_FACE",FACE,{"disambiguationData":[OSD([sQuery(id+"F25.wireOp",EDGE,"E122.top")])]});
            var sketch = newSketch(context, id + "F29", { "sketchPlane" : qUnion([Q0])});
            skLineSegment(sketch, "E125.bottom", {"start": v(-38.1, -990.6) * mm, "end": v(317.5, -990.6) * mm});
            skLineSegment(sketch, "E125.top", {"start": v(-38.1, -355.6) * mm, "end": v(317.5, -355.6) * mm});
            skLineSegment(sketch, "E125.left", {"start": v(-38.1, -990.6) * mm, "end": v(-38.1, -355.6) * mm});
            skLineSegment(sketch, "E125.right", {"start": v(317.5, -990.6) * mm, "end": v(317.5, -355.6) * mm});
            skSolve(sketch);
        }
        {
            var Q0;
            Q0 = qSketchRegion(id + "F29", true);
            extrude(context, id + "F30", {"entities" : qUnion([Q0]), "depth" : 482.6 * mm});
        }
        {
            var Q0;
            Q0=makeQuery(id+"F26.opExtrude","SWEPT_FACE",FACE,{"disambiguationData":[OSD([sQuery(id+"F25.wireOp",EDGE,"E122.left")])]});
            var sketch = newSketch(context, id + "F31", { "sketchPlane" : qUnion([Q0])});
            skLineSegment(sketch, "E126", {"start": v(-609.6, 41.28) * mm, "end": v(-663.48, 41.28) * mm});
            skLineSegment(sketch, "E127", {"start": v(-663.48, 41.28) * mm, "end": v(-1016, 393.8) * mm});
            skLineSegment(sketch, "E128", {"start": v(-1016, 393.8) * mm, "end": v(-1016, 447.68) * mm});
            skLineSegment(sketch, "E129", {"start": v(-1016, 447.68) * mm, "end": v(-609.6, 41.28) * mm});
            skSolve(sketch);
        }
        {
            var Q0;
            Q0 = qSketchRegion(id + "F31", true);
            extrude(context, id + "F32", {"entities" : qUnion([Q0]), "oppositeDirection" : true, "depth" : 19.05 * mm});
        }
        {
            var Q0;
            Q0=makeQuery(id+"F28.opExtrude","CAP_EDGE",EDGE,{"disambiguationData":[OSD([sQuery(id+"F27.wireOp",EDGE,"E123.top")])],"isStart":true});
            cPoint(context, id + "F33", {"entities" : qUnion([Q0]), "parameter" : 0.5});
        }
        {
            var Q0;
            Q0 = qCreatedBy(id + "F33" ,VERTEX);
            var Q1;
            Q1=makeQuery(id+"F30.opExtrude","SWEPT_FACE",FACE,{"disambiguationData":[OSD([sQuery(id+"F29.wireOp",EDGE,"E125.left")])]});
            cPlane(context, id + "F34", {"entities" : qUnion([Q0, Q1]), "cplaneType" : CPlaneType.PLANE_POINT, "offset" : 25.4 * mm, "width" : 152.4 * mm, "height" : 152.4 * mm});
        }
        {
            var Q0;
            Q0=makeQuery(id+"F32.opExtrude","SWEPT_BODY",BODY,{"disambiguationData":[OSD([sQuery(id+"F31.wireOp",EDGE,"E126"),sQuery(id+"F31.wireOp",EDGE,"E127"),sQuery(id+"F31.wireOp",EDGE,"E128"),sQuery(id+"F31.wireOp",EDGE,"E129")])]});
            var Q1;
            Q1=qCreatedBy(id+"F34.planeOp",FACE);
            mirror(context, id + "F35", {"entities" : qUnion([Q0]), "mirrorPlane" : qUnion([Q1])});
        }
    });
